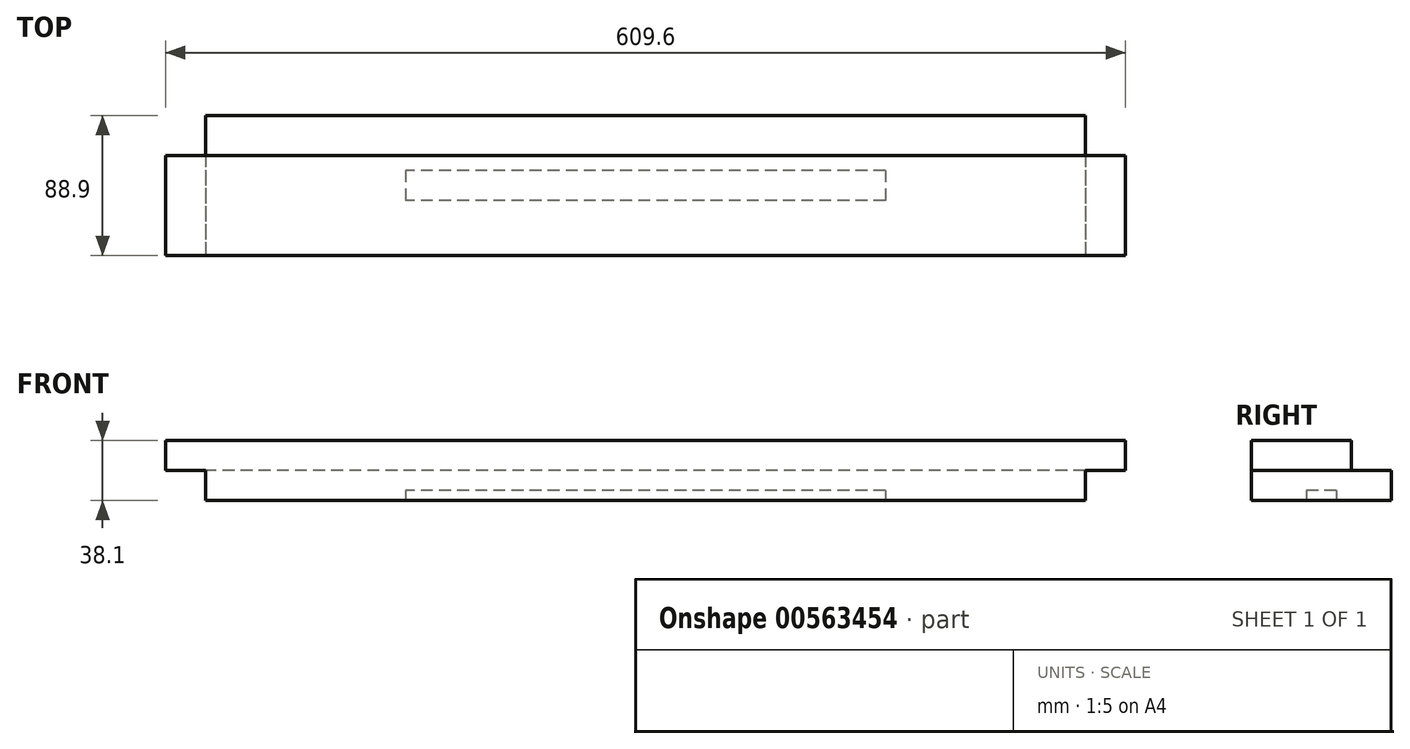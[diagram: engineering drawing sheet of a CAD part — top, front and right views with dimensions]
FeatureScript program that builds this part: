
annotation { "Feature Type Name" : "Feature", "Feature Type Description" : "" }
export const myFeature = defineFeature(function(context is Context, id is Id, definition is map)
    precondition{}
    {
        {
            var Q0;
            Q0=qCreatedBy(makeId("Top.planeOp"),FACE);
            var sketch = newSketch(context, id + "F0", { "sketchPlane" : qUnion([Q0])});
            skLineSegment(sketch, "E0.bottom", {"start": v(-320.57, -18.67) * mm, "end": v(289.03, -18.67) * mm});
            skLineSegment(sketch, "E0.top", {"start": v(-320.57, -107.57) * mm, "end": v(289.03, -107.57) * mm});
            skLineSegment(sketch, "E0.left", {"start": v(-320.57, -18.67) * mm, "end": v(-320.57, -107.57) * mm});
            skLineSegment(sketch, "E0.right", {"start": v(289.03, -18.67) * mm, "end": v(289.03, -107.57) * mm});
            skLineSegment(sketch, "E1", {"start": v(-295.17, -18.67) * mm, "end": v(-295.17, -107.57) * mm});
            skLineSegment(sketch, "E2", {"start": v(263.63, -18.67) * mm, "end": v(263.63, -107.57) * mm});
            skLineSegment(sketch, "E3", {"start": v(-320.57, -44.07) * mm, "end": v(289.03, -44.07) * mm});
            skLineSegment(sketch, "E4.bottom", {"start": v(136.63, -53.6) * mm, "end": v(-168.17, -53.6) * mm});
            skLineSegment(sketch, "E4.top", {"start": v(136.63, -72.65) * mm, "end": v(-168.17, -72.65) * mm});
            skLineSegment(sketch, "E4.left", {"start": v(136.63, -53.6) * mm, "end": v(136.63, -72.65) * mm});
            skLineSegment(sketch, "E4.right", {"start": v(-168.17, -53.6) * mm, "end": v(-168.17, -72.65) * mm});
            skSolve(sketch);
        }
        {
            var Q0;
            {var subQ0=sQuery(id+"F0.wireOp",EDGE,"E1");var subQ1=sQuery(id+"F0.wireOp",EDGE,"E0.top");var subQ2=makeQuery(id+"F0.imprint","INTERSECT",VERTEX,{"derivedFrom":[subQ1,subQ0]});Q0=makeQuery(id+"F0.imprint","IMPRINT",FACE,{"disambiguationData":[TD([[makeQuery(id+"F0.imprint","IMPRINT",EDGE,{"disambiguationData":[TD([[subQ2,-1.0]])],"derivedFrom":subQ1}),1.0]])]});}
            var Q1;
            {var subQ0=sQuery(id+"F0.wireOp",EDGE,"E0.left");var subQ1=sQuery(id+"F0.wireOp",EDGE,"E0.top");var subQ2=makeQuery(id+"F0.imprint","INTERSECT",VERTEX,{"derivedFrom":[subQ1,subQ0]});Q1=makeQuery(id+"F0.imprint","IMPRINT",FACE,{"disambiguationData":[TD([[makeQuery(id+"F0.imprint","IMPRINT",EDGE,{"disambiguationData":[TD([[subQ2,-1.0]])],"derivedFrom":subQ1}),1.0]])]});}
            var Q2;
            {var subQ0=sQuery(id+"F0.wireOp",EDGE,"E1");var subQ1=sQuery(id+"F0.wireOp",EDGE,"E0.bottom");var subQ2=makeQuery(id+"F0.imprint","INTERSECT",VERTEX,{"derivedFrom":[subQ1,subQ0]});Q2=makeQuery(id+"F0.imprint","IMPRINT",FACE,{"disambiguationData":[TD([[makeQuery(id+"F0.imprint","IMPRINT",EDGE,{"disambiguationData":[TD([[subQ2,-1.0]])],"derivedFrom":subQ1}),-1.0]])]});}
            var Q3;
            {var subQ0=sQuery(id+"F0.wireOp",EDGE,"E0.right");var subQ1=sQuery(id+"F0.wireOp",EDGE,"E0.top");var subQ2=makeQuery(id+"F0.imprint","INTERSECT",VERTEX,{"derivedFrom":[subQ1,subQ0]});Q3=makeQuery(id+"F0.imprint","IMPRINT",FACE,{"disambiguationData":[TD([[makeQuery(id+"F0.imprint","IMPRINT",EDGE,{"disambiguationData":[TD([[subQ2,1.0]])],"derivedFrom":subQ1}),1.0]])]});}
            extrude(context, id + "F1", {"entities" : qUnion([Q0, Q1, Q2, Q3]), "depth" : 19.05 * mm, "offsetDistance" : 25.4 * mm});
        }
        {
            var Q0;
            {var subQ0=sQuery(id+"F0.wireOp",EDGE,"E1");var subQ1=sQuery(id+"F0.wireOp",EDGE,"E0.top");var subQ2=makeQuery(id+"F0.imprint","INTERSECT",VERTEX,{"derivedFrom":[subQ1,subQ0]});Q0=makeQuery(id+"F0.imprint","IMPRINT",FACE,{"disambiguationData":[TD([[makeQuery(id+"F0.imprint","IMPRINT",EDGE,{"disambiguationData":[TD([[subQ2,-1.0]])],"derivedFrom":subQ1}),1.0]])]});}
            var Q1;
            {var subQ0=sQuery(id+"F0.wireOp",EDGE,"E0.left");var subQ1=sQuery(id+"F0.wireOp",EDGE,"E0.top");var subQ2=makeQuery(id+"F0.imprint","INTERSECT",VERTEX,{"derivedFrom":[subQ1,subQ0]});Q1=makeQuery(id+"F0.imprint","IMPRINT",FACE,{"disambiguationData":[TD([[makeQuery(id+"F0.imprint","IMPRINT",EDGE,{"disambiguationData":[TD([[subQ2,-1.0]])],"derivedFrom":subQ1}),1.0]])]});}
            var Q2;
            {var subQ0=sQuery(id+"F0.wireOp",EDGE,"E0.right");var subQ1=sQuery(id+"F0.wireOp",EDGE,"E0.top");var subQ2=makeQuery(id+"F0.imprint","INTERSECT",VERTEX,{"derivedFrom":[subQ1,subQ0]});Q2=makeQuery(id+"F0.imprint","IMPRINT",FACE,{"disambiguationData":[TD([[makeQuery(id+"F0.imprint","IMPRINT",EDGE,{"disambiguationData":[TD([[subQ2,1.0]])],"derivedFrom":subQ1}),1.0]])]});}
            extrude(context, id + "F2", {"entities" : qUnion([Q0, Q1, Q2]), "operationType" : NewBodyOperationType.ADD, "depth" : 38.1 * mm, "offsetDistance" : 25.4 * mm});
        }
        {
            var Q0;
            {var subQ0=sQuery(id+"F0.wireOp",EDGE,"E0.left");var subQ1=sQuery(id+"F0.wireOp",EDGE,"E0.top");var subQ2=makeQuery(id+"F0.imprint","INTERSECT",VERTEX,{"derivedFrom":[subQ1,subQ0]});Q0=makeQuery(id+"F0.imprint","IMPRINT",FACE,{"disambiguationData":[TD([[makeQuery(id+"F0.imprint","IMPRINT",EDGE,{"disambiguationData":[TD([[subQ2,-1.0]])],"derivedFrom":subQ1}),1.0]])]});}
            var Q1;
            {var subQ0=sQuery(id+"F0.wireOp",EDGE,"E0.right");var subQ1=sQuery(id+"F0.wireOp",EDGE,"E0.top");var subQ2=makeQuery(id+"F0.imprint","INTERSECT",VERTEX,{"derivedFrom":[subQ1,subQ0]});Q1=makeQuery(id+"F0.imprint","IMPRINT",FACE,{"disambiguationData":[TD([[makeQuery(id+"F0.imprint","IMPRINT",EDGE,{"disambiguationData":[TD([[subQ2,1.0]])],"derivedFrom":subQ1}),1.0]])]});}
            extrude(context, id + "F3", {"entities" : qUnion([Q0, Q1]), "operationType" : NewBodyOperationType.REMOVE, "oppositeDirection" : true, "depth" : -19.05 * mm, "offsetDistance" : 25.4 * mm});
        }
        {
            var Q0;
            Q0=makeQuery(id+"F0.imprint","IMPRINT",FACE,{"disambiguationData":[TD([[makeQuery(id+"F0.imprint","IMPRINT",EDGE,{"derivedFrom":sQuery(id+"F0.wireOp",EDGE,"E4.bottom")}),1.0]])]});
            extrude(context, id + "F4", {"entities" : qUnion([Q0]), "operationType" : NewBodyOperationType.ADD, "depth" : 38.1 * mm, "offsetDistance" : 25.4 * mm});
        }
        {
            var Q0;
            Q0=makeQuery(id+"F0.imprint","IMPRINT",FACE,{"disambiguationData":[TD([[makeQuery(id+"F0.imprint","IMPRINT",EDGE,{"derivedFrom":sQuery(id+"F0.wireOp",EDGE,"E4.bottom")}),1.0]])]});
            extrude(context, id + "F5", {"entities" : qUnion([Q0]), "operationType" : NewBodyOperationType.REMOVE, "oppositeDirection" : true, "depth" : -6.35 * mm, "offsetDistance" : 25.4 * mm});
        }
    });
